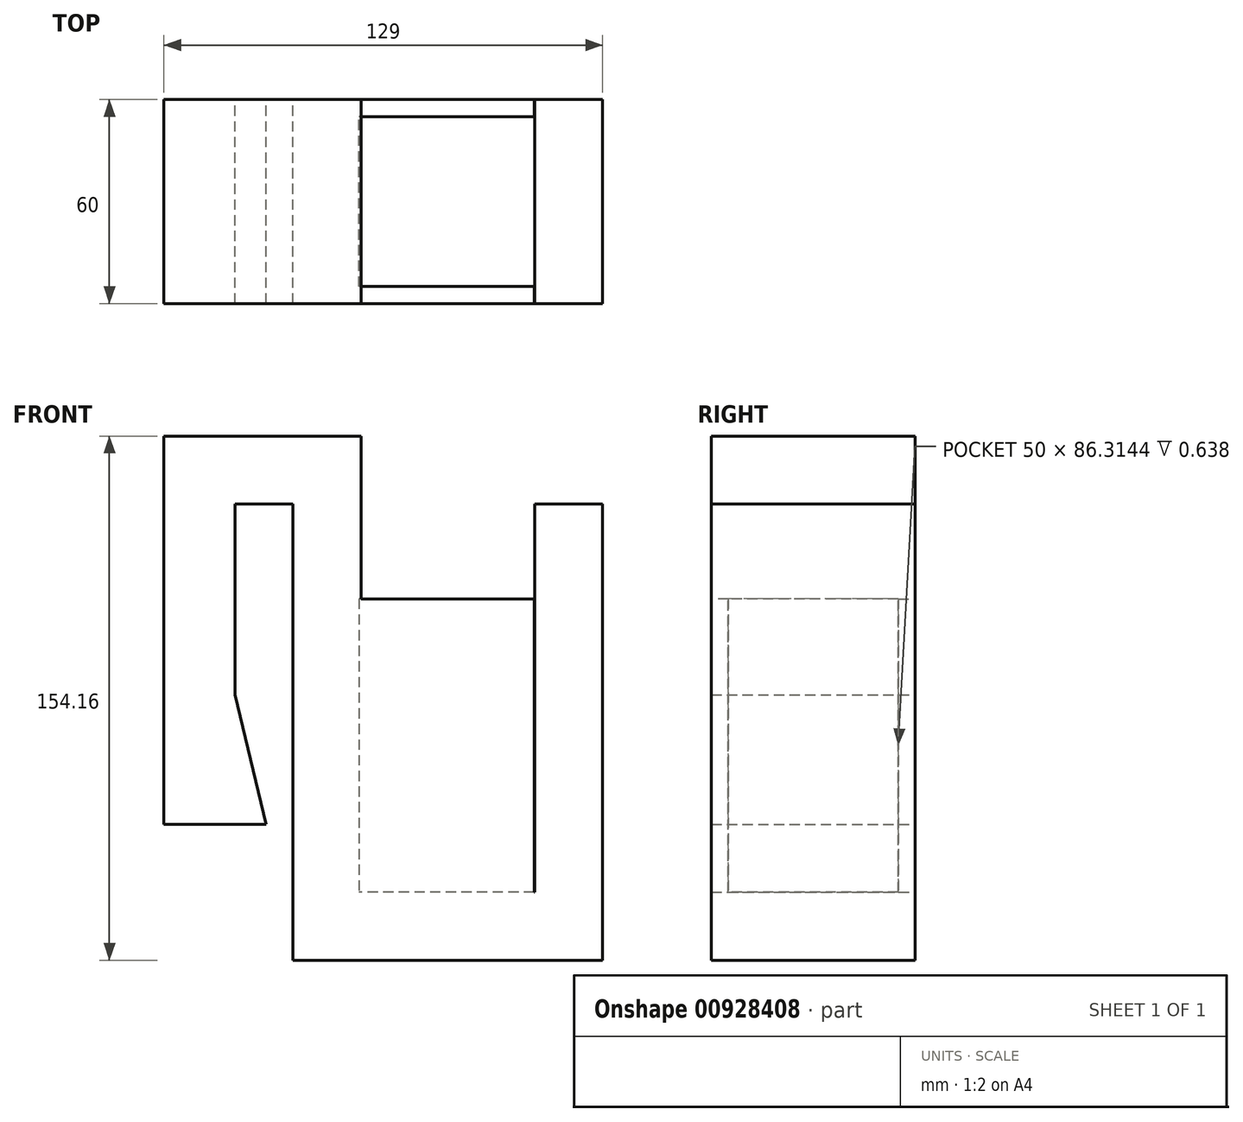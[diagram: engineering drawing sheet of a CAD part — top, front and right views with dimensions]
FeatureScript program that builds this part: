
annotation { "Feature Type Name" : "Feature", "Feature Type Description" : "" }
export const myFeature = defineFeature(function(context is Context, id is Id, definition is map)
    precondition{}
    {
        {
            var Q0;
            Q0=qCreatedBy(makeId("Front.planeOp"),FACE);
            var sketch = newSketch(context, id + "F0", { "sketchPlane" : qUnion([Q0])});
            skLineSegment(sketch, "E0", {"start": v(-31.68, 38.11) * mm, "end": v(-31.68, 94.17) * mm});
            skLineSegment(sketch, "E1", {"start": v(-31.68, 94.17) * mm, "end": v(-14.56, 94.17) * mm});
            skLineSegment(sketch, "E2", {"start": v(-14.56, 94.17) * mm, "end": v(-14.56, -40) * mm});
            skLineSegment(sketch, "E3", {"start": v(-14.56, -40) * mm, "end": v(76.44, -40) * mm});
            skLineSegment(sketch, "E4", {"start": v(76.44, -40) * mm, "end": v(76.44, 94.17) * mm});
            skLineSegment(sketch, "E5", {"start": v(76.44, 94.17) * mm, "end": v(56.44, 94.17) * mm});
            skLineSegment(sketch, "E6", {"start": v(56.44, 94.17) * mm, "end": v(56.44, -20) * mm});
            skLineSegment(sketch, "E7", {"start": v(56.44, -20) * mm, "end": v(5.44, -20) * mm});
            skLineSegment(sketch, "E8", {"start": v(5.44, -20) * mm, "end": v(5.44, 114.17) * mm});
            skLineSegment(sketch, "E9", {"start": v(5.44, 114.17) * mm, "end": v(-52.56, 114.17) * mm});
            skLineSegment(sketch, "E10", {"start": v(-52.56, 114.17) * mm, "end": v(-52.56, 0) * mm});
            skLineSegment(sketch, "E11", {"start": v(-52.56, 0) * mm, "end": v(-22.56, 0) * mm});
            skLineSegment(sketch, "E12", {"start": v(-31.68, 38.11) * mm, "end": v(-22.56, 0) * mm});
            skSolve(sketch);
        }
        {
            var Q0;
            Q0 = qSketchRegion(id + "F0", true);
            extrude(context, id + "F1", {"entities" : qUnion([Q0]), "endBound" : BoundingType.SYMMETRIC, "depth" : 60 * mm, "offsetDistance" : 25.4 * mm});
        }
        {
            var Q0;
            Q0=qCreatedBy(makeId("Front.planeOp"),FACE);
            var sketch = newSketch(context, id + "F2", { "sketchPlane" : qUnion([Q0])});
            skLineSegment(sketch, "E13.bottom", {"start": v(56.34, -20) * mm, "end": v(-14.56, -20) * mm});
            skLineSegment(sketch, "E13.top", {"start": v(56.34, 66.32) * mm, "end": v(-14.56, 66.32) * mm});
            skLineSegment(sketch, "E13.left", {"start": v(56.34, -20) * mm, "end": v(56.34, 66.32) * mm});
            skLineSegment(sketch, "E13.right", {"start": v(-14.56, -20) * mm, "end": v(-14.56, 66.32) * mm});
            skLineSegment(sketch, "E14", {"start": v(4.8, 66.32) * mm, "end": v(4.8, -20) * mm});
            skSolve(sketch);
        }
        {
            var Q0;
            Q0 = qSketchRegion(id + "F2", true);
            extrude(context, id + "F3", {"entities" : qUnion([Q0]), "operationType" : NewBodyOperationType.ADD, "endBound" : BoundingType.SYMMETRIC, "depth" : 60 * mm, "offsetDistance" : 25.4 * mm});
        }
        {
            var Q0;
            {var subQ0=sQuery(id+"F2.wireOp",EDGE,"E13.left");Q0=makeQuery(id+"F2.imprint","IMPRINT",FACE,{"disambiguationData":[TD([[makeQuery(id+"F2.imprint","IMPRINT",EDGE,{"derivedFrom":subQ0}),1.0]])]});}
            extrude(context, id + "F4", {"entities" : qUnion([Q0]), "operationType" : NewBodyOperationType.REMOVE, "endBound" : BoundingType.SYMMETRIC, "depth" : 50 * mm, "offsetDistance" : 25.4 * mm});
        }
    });
